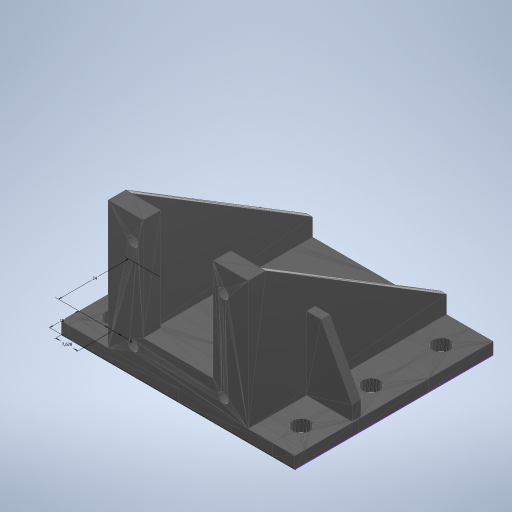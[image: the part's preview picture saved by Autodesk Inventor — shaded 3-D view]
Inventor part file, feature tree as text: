
AUTODESK INVENTOR PART (.ipt)
format: ipt  version: 2023 (Build 270158000, 158)  size: 256,512 bytes
history: native  units: mm
features: other x2, sketch x1
ambient origin geometry x8: Origin, YZ Plane, XZ Plane, XY Plane, X Axis, Y Axis, Z Axis, Center Point
feature tree (3):
  other  "nema17bracket"
  sketch  "Boceto1"  dims[d0=6.0mm d1=10.00003mm d2=24.000123mm d3=7.628278mm]
  other  "MeshFeature1"
